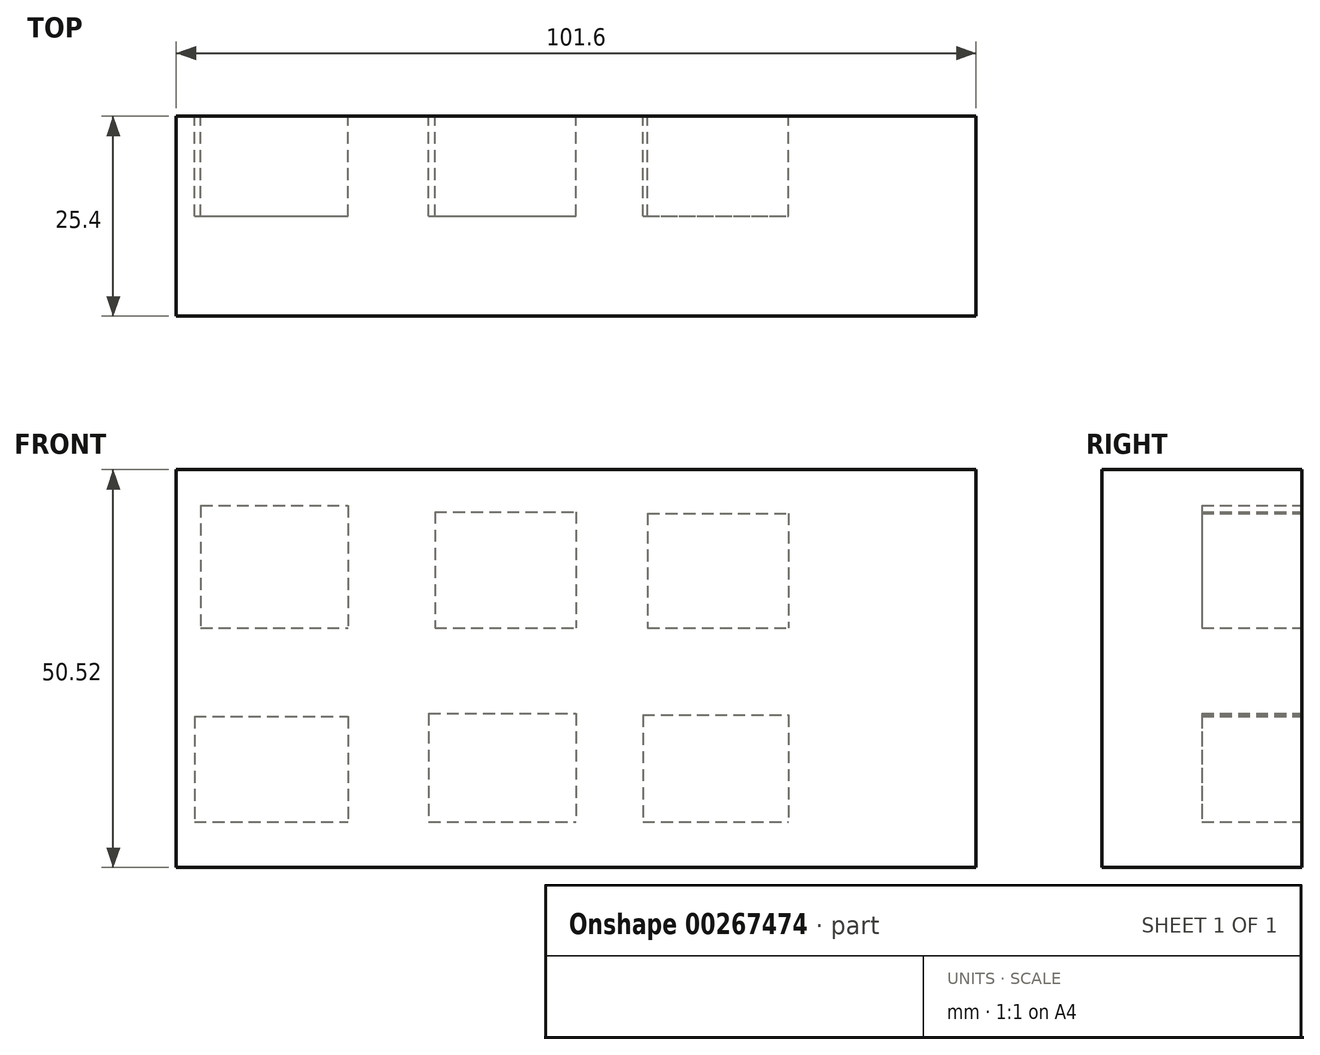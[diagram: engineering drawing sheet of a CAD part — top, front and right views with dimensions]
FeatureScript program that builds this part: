
annotation { "Feature Type Name" : "Feature", "Feature Type Description" : "" }
export const myFeature = defineFeature(function(context is Context, id is Id, definition is map)
    precondition{}
    {
        {
            var Q0;
            Q0=qCreatedBy(makeId("Front.planeOp"),FACE);
            var sketch = newSketch(context, id + "F0", { "sketchPlane" : qUnion([Q0])});
            skLineSegment(sketch, "E0.bottom", {"start": v(50.8, 25.26) * mm, "end": v(-50.8, 25.26) * mm});
            skLineSegment(sketch, "E0.top", {"start": v(50.8, -25.26) * mm, "end": v(-50.8, -25.26) * mm});
            skLineSegment(sketch, "E0.left", {"start": v(50.8, 25.26) * mm, "end": v(50.8, -25.26) * mm});
            skLineSegment(sketch, "E0.right", {"start": v(-50.8, 25.26) * mm, "end": v(-50.8, -25.26) * mm});
            skPoint(sketch, "E0.middle", {"position": v(0, 0) * mm});
            skLineSegment(sketch, "E1.bottom", {"start": v(-47.7, 20.7) * mm, "end": v(-28.97, 20.7) * mm});
            skLineSegment(sketch, "E1.top", {"start": v(-47.7, 5.12) * mm, "end": v(-28.97, 5.12) * mm});
            skLineSegment(sketch, "E1.left", {"start": v(-47.7, 20.7) * mm, "end": v(-47.7, 5.12) * mm});
            skLineSegment(sketch, "E1.right", {"start": v(-28.97, 20.7) * mm, "end": v(-28.97, 5.12) * mm});
            skLineSegment(sketch, "E2.bottom", {"start": v(-48.48, -6.1) * mm, "end": v(-28.97, -6.1) * mm});
            skLineSegment(sketch, "E2.top", {"start": v(-48.48, -19.5) * mm, "end": v(-28.97, -19.5) * mm});
            skLineSegment(sketch, "E2.left", {"start": v(-48.48, -6.1) * mm, "end": v(-48.48, -19.5) * mm});
            skLineSegment(sketch, "E2.right", {"start": v(-28.97, -6.1) * mm, "end": v(-28.97, -19.5) * mm});
            skLineSegment(sketch, "E3.bottom", {"start": v(-17.93, 19.9) * mm, "end": v(0, 19.9) * mm});
            skLineSegment(sketch, "E3.top", {"start": v(-17.93, 5.12) * mm, "end": v(0, 5.12) * mm});
            skLineSegment(sketch, "E3.left", {"start": v(-17.93, 19.9) * mm, "end": v(-17.93, 5.12) * mm});
            skLineSegment(sketch, "E3.right", {"start": v(0, 19.9) * mm, "end": v(0, 5.12) * mm});
            skLineSegment(sketch, "E4.bottom", {"start": v(-18.72, -5.72) * mm, "end": v(0, -5.72) * mm});
            skLineSegment(sketch, "E4.top", {"start": v(-18.72, -19.5) * mm, "end": v(0, -19.5) * mm});
            skLineSegment(sketch, "E4.left", {"start": v(-18.72, -5.72) * mm, "end": v(-18.72, -19.5) * mm});
            skLineSegment(sketch, "E4.right", {"start": v(0, -5.72) * mm, "end": v(0, -19.5) * mm});
            skLineSegment(sketch, "E5.bottom", {"start": v(9.07, 19.7) * mm, "end": v(27, 19.7) * mm});
            skLineSegment(sketch, "E5.top", {"start": v(9.07, 5.12) * mm, "end": v(27, 5.12) * mm});
            skLineSegment(sketch, "E5.left", {"start": v(9.07, 19.7) * mm, "end": v(9.07, 5.12) * mm});
            skLineSegment(sketch, "E5.right", {"start": v(27, 19.7) * mm, "end": v(27, 5.12) * mm});
            skLineSegment(sketch, "E6.bottom", {"start": v(8.47, -5.91) * mm, "end": v(27, -5.91) * mm});
            skLineSegment(sketch, "E6.top", {"start": v(8.47, -19.5) * mm, "end": v(27, -19.5) * mm});
            skLineSegment(sketch, "E6.left", {"start": v(8.47, -5.91) * mm, "end": v(8.47, -19.5) * mm});
            skLineSegment(sketch, "E6.right", {"start": v(27, -5.91) * mm, "end": v(27, -19.5) * mm});
            skSolve(sketch);
        }
        {
            var Q0;
            Q0 = qSketchRegion(id + "F0", true);
            var Q1;
            Q1=makeQuery(id+"F0.imprint","IMPRINT",FACE,{"disambiguationData":[TD([[makeQuery(id+"F0.imprint","IMPRINT",EDGE,{"derivedFrom":sQuery(id+"F0.wireOp",EDGE,"E1.bottom")}),-1.0]])]});
            var Q2;
            Q2=makeQuery(id+"F0.imprint","IMPRINT",FACE,{"disambiguationData":[TD([[makeQuery(id+"F0.imprint","IMPRINT",EDGE,{"derivedFrom":sQuery(id+"F0.wireOp",EDGE,"E3.bottom")}),-1.0]])]});
            var Q3;
            Q3=makeQuery(id+"F0.imprint","IMPRINT",FACE,{"disambiguationData":[TD([[makeQuery(id+"F0.imprint","IMPRINT",EDGE,{"derivedFrom":sQuery(id+"F0.wireOp",EDGE,"E5.bottom")}),-1.0]])]});
            var Q4;
            Q4=makeQuery(id+"F0.imprint","IMPRINT",FACE,{"disambiguationData":[TD([[makeQuery(id+"F0.imprint","IMPRINT",EDGE,{"derivedFrom":sQuery(id+"F0.wireOp",EDGE,"E6.bottom")}),-1.0]])]});
            var Q5;
            Q5=makeQuery(id+"F0.imprint","IMPRINT",FACE,{"disambiguationData":[TD([[makeQuery(id+"F0.imprint","IMPRINT",EDGE,{"derivedFrom":sQuery(id+"F0.wireOp",EDGE,"E4.bottom")}),-1.0]])]});
            var Q6;
            Q6=makeQuery(id+"F0.imprint","IMPRINT",FACE,{"disambiguationData":[TD([[makeQuery(id+"F0.imprint","IMPRINT",EDGE,{"derivedFrom":sQuery(id+"F0.wireOp",EDGE,"E2.bottom")}),-1.0]])]});
            extrude(context, id + "F1", {"entities" : qUnion([Q0, Q1, Q2, Q3, Q4, Q5, Q6]), "depth" : 25.4 * mm});
        }
        {
            var Q0;
            Q0=makeQuery(id+"F0.imprint","IMPRINT",FACE,{"disambiguationData":[TD([[makeQuery(id+"F0.imprint","IMPRINT",EDGE,{"derivedFrom":sQuery(id+"F0.wireOp",EDGE,"E1.bottom")}),-1.0]])]});
            var Q1;
            Q1=makeQuery(id+"F0.imprint","IMPRINT",FACE,{"disambiguationData":[TD([[makeQuery(id+"F0.imprint","IMPRINT",EDGE,{"derivedFrom":sQuery(id+"F0.wireOp",EDGE,"E3.bottom")}),-1.0]])]});
            var Q2;
            Q2=makeQuery(id+"F0.imprint","IMPRINT",FACE,{"disambiguationData":[TD([[makeQuery(id+"F0.imprint","IMPRINT",EDGE,{"derivedFrom":sQuery(id+"F0.wireOp",EDGE,"E5.bottom")}),-1.0]])]});
            var Q3;
            Q3=makeQuery(id+"F0.imprint","IMPRINT",FACE,{"disambiguationData":[TD([[makeQuery(id+"F0.imprint","IMPRINT",EDGE,{"derivedFrom":sQuery(id+"F0.wireOp",EDGE,"E6.bottom")}),-1.0]])]});
            var Q4;
            Q4=makeQuery(id+"F0.imprint","IMPRINT",FACE,{"disambiguationData":[TD([[makeQuery(id+"F0.imprint","IMPRINT",EDGE,{"derivedFrom":sQuery(id+"F0.wireOp",EDGE,"E4.bottom")}),-1.0]])]});
            var Q5;
            Q5=makeQuery(id+"F0.imprint","IMPRINT",FACE,{"disambiguationData":[TD([[makeQuery(id+"F0.imprint","IMPRINT",EDGE,{"derivedFrom":sQuery(id+"F0.wireOp",EDGE,"E2.bottom")}),-1.0]])]});
            extrude(context, id + "F2", {"entities" : qUnion([Q0, Q1, Q2, Q3, Q4, Q5]), "operationType" : NewBodyOperationType.REMOVE, "depth" : 12.7 * mm});
        }
    });
